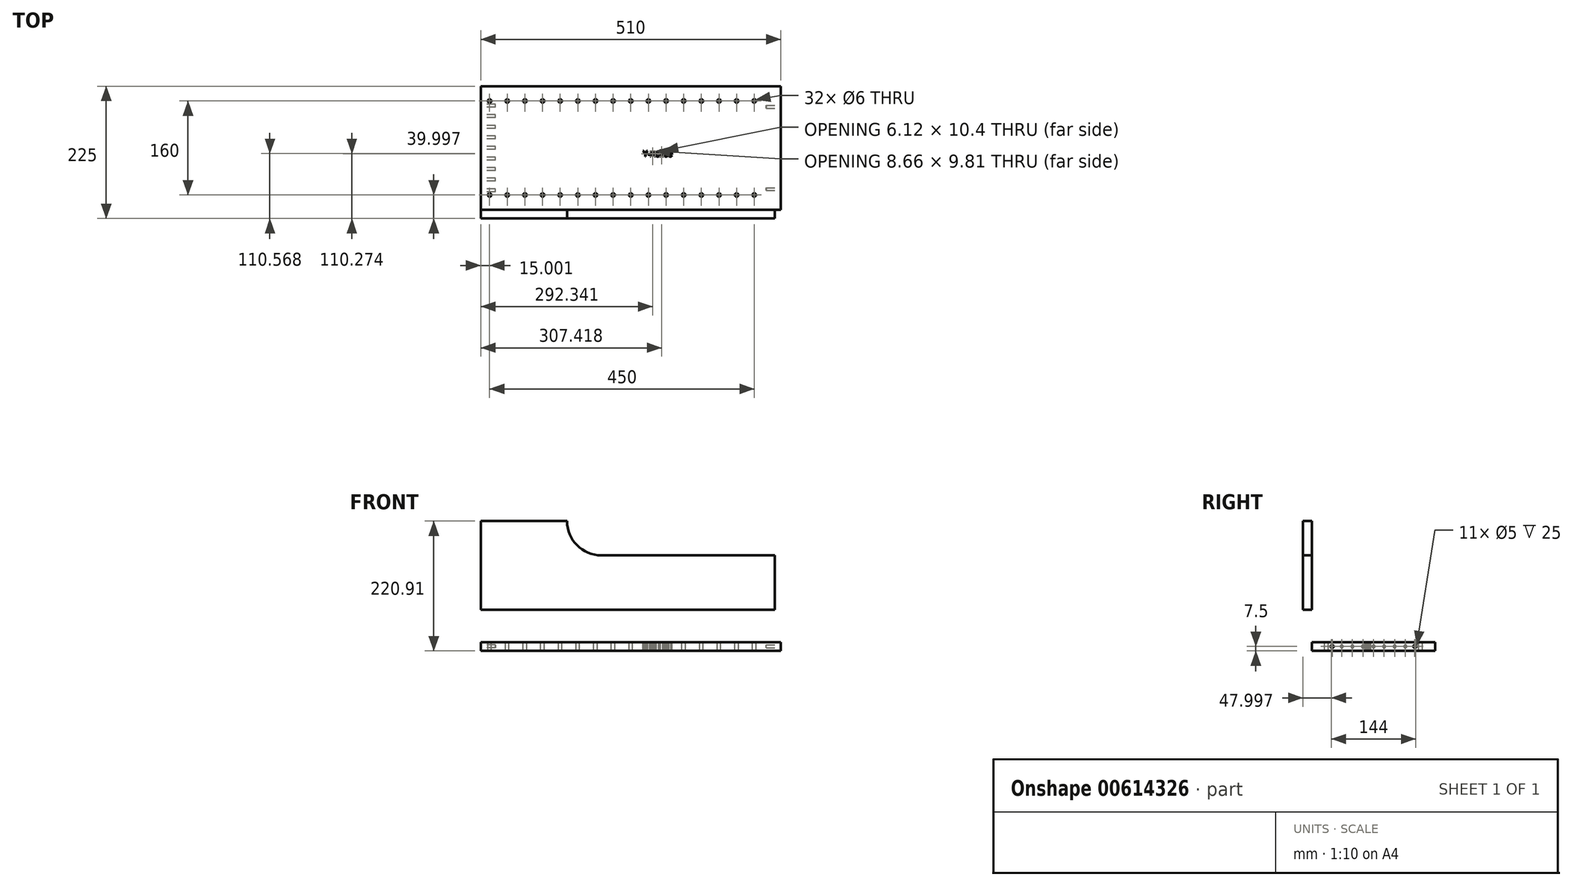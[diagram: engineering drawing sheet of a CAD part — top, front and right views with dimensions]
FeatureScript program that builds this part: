
annotation { "Feature Type Name" : "Feature", "Feature Type Description" : "" }
export const myFeature = defineFeature(function(context is Context, id is Id, definition is map)
    precondition{}
    {
        {
            var Q0;
            Q0=qCreatedBy(makeId("Top.planeOp"),FACE);
            var sketch = newSketch(context, id + "F0", { "sketchPlane" : qUnion([Q0])});
            skLineSegment(sketch, "E0.bottom", {"start": v(2.5, 35.14) * mm, "end": v(512.5, 35.14) * mm});
            skLineSegment(sketch, "E0.top", {"start": v(2.5, 245.14) * mm, "end": v(512.5, 245.14) * mm});
            skLineSegment(sketch, "E0.left", {"start": v(2.5, 35.14) * mm, "end": v(2.5, 245.14) * mm});
            skLineSegment(sketch, "E0.right", {"start": v(512.5, 35.14) * mm, "end": v(512.5, 245.14) * mm});
            skCircle(sketch, "E1", {"center": v(17.5, 60.14) * mm, "radius": 3 * mm});
            skCircle(sketch, "E2.0.1.1", {"center": v(17.5, 220.14) * mm, "radius": 3 * mm});
            skCircle(sketch, "E2.1.0.1", {"center": v(47.5, 60.14) * mm, "radius": 3 * mm});
            skCircle(sketch, "E2.1.1.1", {"center": v(47.5, 220.14) * mm, "radius": 3 * mm});
            skCircle(sketch, "E2.2.0.1", {"center": v(77.5, 60.14) * mm, "radius": 3 * mm});
            skCircle(sketch, "E2.2.1.1", {"center": v(77.5, 220.14) * mm, "radius": 3 * mm});
            skCircle(sketch, "E2.3.0.1", {"center": v(107.5, 60.14) * mm, "radius": 3 * mm});
            skCircle(sketch, "E2.3.1.1", {"center": v(107.5, 220.14) * mm, "radius": 3 * mm});
            skCircle(sketch, "E2.4.0.1", {"center": v(137.5, 60.14) * mm, "radius": 3 * mm});
            skCircle(sketch, "E2.4.1.1", {"center": v(137.5, 220.14) * mm, "radius": 3 * mm});
            skCircle(sketch, "E2.5.0.1", {"center": v(167.5, 60.14) * mm, "radius": 3 * mm});
            skCircle(sketch, "E2.5.1.1", {"center": v(167.5, 220.14) * mm, "radius": 3 * mm});
            skCircle(sketch, "E2.6.0.1", {"center": v(197.5, 60.14) * mm, "radius": 3 * mm});
            skCircle(sketch, "E2.6.1.1", {"center": v(197.5, 220.14) * mm, "radius": 3 * mm});
            skCircle(sketch, "E2.7.0.1", {"center": v(227.5, 60.14) * mm, "radius": 3 * mm});
            skCircle(sketch, "E2.7.1.1", {"center": v(227.5, 220.14) * mm, "radius": 3 * mm});
            skCircle(sketch, "E2.8.0.1", {"center": v(257.5, 60.14) * mm, "radius": 3 * mm});
            skCircle(sketch, "E2.8.1.1", {"center": v(257.5, 220.14) * mm, "radius": 3 * mm});
            skCircle(sketch, "E2.9.0.1", {"center": v(287.5, 60.14) * mm, "radius": 3 * mm});
            skCircle(sketch, "E2.9.1.1", {"center": v(287.5, 220.14) * mm, "radius": 3 * mm});
            skCircle(sketch, "E2.10.0.1", {"center": v(317.5, 60.14) * mm, "radius": 3 * mm});
            skCircle(sketch, "E2.10.1.1", {"center": v(317.5, 220.14) * mm, "radius": 3 * mm});
            skCircle(sketch, "E2.11.0.1", {"center": v(347.5, 60.14) * mm, "radius": 3 * mm});
            skCircle(sketch, "E2.11.1.1", {"center": v(347.5, 220.14) * mm, "radius": 3 * mm});
            skCircle(sketch, "E2.12.0.1", {"center": v(377.5, 60.14) * mm, "radius": 3 * mm});
            skCircle(sketch, "E2.12.1.1", {"center": v(377.5, 220.14) * mm, "radius": 3 * mm});
            skCircle(sketch, "E2.13.0.1", {"center": v(407.5, 60.14) * mm, "radius": 3 * mm});
            skCircle(sketch, "E2.13.1.1", {"center": v(407.5, 220.14) * mm, "radius": 3 * mm});
            skCircle(sketch, "E2.14.0.1", {"center": v(437.5, 60.14) * mm, "radius": 3 * mm});
            skCircle(sketch, "E2.14.1.1", {"center": v(437.5, 220.14) * mm, "radius": 3 * mm});
            skLineSegment(sketch, "E2.direction1", {"start": v(17.5, 60.14) * mm, "end": v(47.5, 60.14) * mm, "construction": true});
            skLineSegment(sketch, "E2.direction2", {"start": v(17.5, 60.14) * mm, "end": v(17.5, 220.14) * mm, "construction": true});
            skText(sketch, "E3", { "text": "Y-Achse", "fontName": "OpenSans-Regular.ttf"});
            skCircle(sketch, "E4.2.15.0", {"center": v(467.5, 60.14) * mm, "radius": 3 * mm});
            skCircle(sketch, "E4.2.15.1", {"center": v(467.5, 220.14) * mm, "radius": 3 * mm});
            skPoint(sketch, "E5", {"position": v(17.5, 140.14) * mm});
            skPoint(sketch, "E6", {"position": v(2.5, 140.14) * mm});
            const initialGuessF0  = {"E3": [0.27844, 0.12551, 1, 0, 0.00985]};
            skSetInitialGuess(sketch, initialGuessF0);
            skSolve(sketch);
        }
        {
            var Q0;
            Q0=makeQuery(id+"F0.imprint","IMPRINT",FACE,{"disambiguationData":[TD([[makeQuery(id+"F0.imprint","IMPRINT",EDGE,{"derivedFrom":sQuery(id+"F0.wireOp",EDGE,"E1")}),-1.0]])]});
            var Q1;
            Q1=makeQuery(id+"F0.imprint","IMPRINT",FACE,{"disambiguationData":[TD([[makeQuery(id+"F0.imprint","IMPRINT",EDGE,{"derivedFrom":sQuery(id+"F0.wireOp",EDGE,"E2.1.0.0")}),1.0]])]});
            var Q2;
            Q2=makeQuery(id+"F0.imprint","IMPRINT",FACE,{"disambiguationData":[TD([[makeQuery(id+"F0.imprint","IMPRINT",EDGE,{"derivedFrom":sQuery(id+"F0.wireOp",EDGE,"E2.2.0.0")}),1.0]])]});
            var Q3;
            Q3=makeQuery(id+"F0.imprint","IMPRINT",FACE,{"disambiguationData":[TD([[makeQuery(id+"F0.imprint","IMPRINT",EDGE,{"derivedFrom":sQuery(id+"F0.wireOp",EDGE,"E2.3.0.0")}),1.0]])]});
            var Q4;
            Q4=makeQuery(id+"F0.imprint","IMPRINT",FACE,{"disambiguationData":[TD([[makeQuery(id+"F0.imprint","IMPRINT",EDGE,{"derivedFrom":sQuery(id+"F0.wireOp",EDGE,"E2.0.1.0")}),1.0]])]});
            var Q5;
            Q5=makeQuery(id+"F0.imprint","IMPRINT",FACE,{"disambiguationData":[TD([[makeQuery(id+"F0.imprint","IMPRINT",EDGE,{"derivedFrom":sQuery(id+"F0.wireOp",EDGE,"E2.1.1.0")}),1.0]])]});
            var Q6;
            Q6=makeQuery(id+"F0.imprint","IMPRINT",FACE,{"disambiguationData":[TD([[makeQuery(id+"F0.imprint","IMPRINT",EDGE,{"derivedFrom":sQuery(id+"F0.wireOp",EDGE,"E2.2.1.0")}),1.0]])]});
            var Q7;
            Q7=makeQuery(id+"F0.imprint","IMPRINT",FACE,{"disambiguationData":[TD([[makeQuery(id+"F0.imprint","IMPRINT",EDGE,{"derivedFrom":sQuery(id+"F0.wireOp",EDGE,"E2.3.1.0")}),1.0]])]});
            var Q8;
            Q8=makeQuery(id+"F0.imprint","IMPRINT",FACE,{"disambiguationData":[TD([[makeQuery(id+"F0.imprint","IMPRINT",EDGE,{"derivedFrom":sQuery(id+"F0.wireOp",EDGE,"E2.4.1.0")}),1.0]])]});
            var Q9;
            Q9=makeQuery(id+"F0.imprint","IMPRINT",FACE,{"disambiguationData":[TD([[makeQuery(id+"F0.imprint","IMPRINT",EDGE,{"derivedFrom":sQuery(id+"F0.wireOp",EDGE,"E2.5.1.0")}),1.0]])]});
            var Q10;
            Q10=makeQuery(id+"F0.imprint","IMPRINT",FACE,{"disambiguationData":[TD([[makeQuery(id+"F0.imprint","IMPRINT",EDGE,{"derivedFrom":sQuery(id+"F0.wireOp",EDGE,"E2.6.1.0")}),1.0]])]});
            var Q11;
            Q11=makeQuery(id+"F0.imprint","IMPRINT",FACE,{"disambiguationData":[TD([[makeQuery(id+"F0.imprint","IMPRINT",EDGE,{"derivedFrom":sQuery(id+"F0.wireOp",EDGE,"E2.7.1.0")}),1.0]])]});
            var Q12;
            Q12=makeQuery(id+"F0.imprint","IMPRINT",FACE,{"disambiguationData":[TD([[makeQuery(id+"F0.imprint","IMPRINT",EDGE,{"derivedFrom":sQuery(id+"F0.wireOp",EDGE,"E2.8.1.0")}),1.0]])]});
            var Q13;
            Q13=makeQuery(id+"F0.imprint","IMPRINT",FACE,{"disambiguationData":[TD([[makeQuery(id+"F0.imprint","IMPRINT",EDGE,{"derivedFrom":sQuery(id+"F0.wireOp",EDGE,"E2.10.1.0")}),1.0]])]});
            var Q14;
            Q14=makeQuery(id+"F0.imprint","IMPRINT",FACE,{"disambiguationData":[TD([[makeQuery(id+"F0.imprint","IMPRINT",EDGE,{"derivedFrom":sQuery(id+"F0.wireOp",EDGE,"E2.9.1.0")}),1.0]])]});
            var Q15;
            Q15=makeQuery(id+"F0.imprint","IMPRINT",FACE,{"disambiguationData":[TD([[makeQuery(id+"F0.imprint","IMPRINT",EDGE,{"derivedFrom":sQuery(id+"F0.wireOp",EDGE,"E2.11.1.0")}),1.0]])]});
            var Q16;
            Q16=makeQuery(id+"F0.imprint","IMPRINT",FACE,{"disambiguationData":[TD([[makeQuery(id+"F0.imprint","IMPRINT",EDGE,{"derivedFrom":sQuery(id+"F0.wireOp",EDGE,"E2.12.1.0")}),1.0]])]});
            var Q17;
            Q17=makeQuery(id+"F0.imprint","IMPRINT",FACE,{"disambiguationData":[TD([[makeQuery(id+"F0.imprint","IMPRINT",EDGE,{"derivedFrom":sQuery(id+"F0.wireOp",EDGE,"E2.13.1.0")}),1.0]])]});
            var Q18;
            Q18=makeQuery(id+"F0.imprint","IMPRINT",FACE,{"disambiguationData":[TD([[makeQuery(id+"F0.imprint","IMPRINT",EDGE,{"derivedFrom":sQuery(id+"F0.wireOp",EDGE,"E2.14.1.0")}),1.0]])]});
            var Q19;
            Q19=makeQuery(id+"F0.imprint","IMPRINT",FACE,{"disambiguationData":[TD([[makeQuery(id+"F0.imprint","IMPRINT",EDGE,{"derivedFrom":sQuery(id+"F0.wireOp",EDGE,"E2.15.1.0")}),1.0]])]});
            var Q20;
            Q20=makeQuery(id+"F0.imprint","IMPRINT",FACE,{"disambiguationData":[TD([[makeQuery(id+"F0.imprint","IMPRINT",EDGE,{"derivedFrom":sQuery(id+"F0.wireOp",EDGE,"E2.16.1.0")}),1.0]])]});
            var Q21;
            Q21=makeQuery(id+"F0.imprint","IMPRINT",FACE,{"disambiguationData":[TD([[makeQuery(id+"F0.imprint","IMPRINT",EDGE,{"derivedFrom":sQuery(id+"F0.wireOp",EDGE,"E2.17.1.0")}),1.0]])]});
            var Q22;
            Q22=makeQuery(id+"F0.imprint","IMPRINT",FACE,{"disambiguationData":[TD([[makeQuery(id+"F0.imprint","IMPRINT",EDGE,{"derivedFrom":sQuery(id+"F0.wireOp",EDGE,"E2.18.1.0")}),1.0]])]});
            var Q23;
            Q23=makeQuery(id+"F0.imprint","IMPRINT",FACE,{"disambiguationData":[TD([[makeQuery(id+"F0.imprint","IMPRINT",EDGE,{"derivedFrom":sQuery(id+"F0.wireOp",EDGE,"E2.19.1.0")}),1.0]])]});
            var Q24;
            Q24=makeQuery(id+"F0.imprint","IMPRINT",FACE,{"disambiguationData":[TD([[makeQuery(id+"F0.imprint","IMPRINT",EDGE,{"derivedFrom":sQuery(id+"F0.wireOp",EDGE,"E2.19.0.0")}),1.0]])]});
            var Q25;
            Q25=makeQuery(id+"F0.imprint","IMPRINT",FACE,{"disambiguationData":[TD([[makeQuery(id+"F0.imprint","IMPRINT",EDGE,{"derivedFrom":sQuery(id+"F0.wireOp",EDGE,"E2.18.0.0")}),1.0]])]});
            var Q26;
            Q26=makeQuery(id+"F0.imprint","IMPRINT",FACE,{"disambiguationData":[TD([[makeQuery(id+"F0.imprint","IMPRINT",EDGE,{"derivedFrom":sQuery(id+"F0.wireOp",EDGE,"E2.17.0.0")}),1.0]])]});
            var Q27;
            Q27=makeQuery(id+"F0.imprint","IMPRINT",FACE,{"disambiguationData":[TD([[makeQuery(id+"F0.imprint","IMPRINT",EDGE,{"derivedFrom":sQuery(id+"F0.wireOp",EDGE,"E2.16.0.0")}),1.0]])]});
            var Q28;
            Q28=makeQuery(id+"F0.imprint","IMPRINT",FACE,{"disambiguationData":[TD([[makeQuery(id+"F0.imprint","IMPRINT",EDGE,{"derivedFrom":sQuery(id+"F0.wireOp",EDGE,"E2.15.0.0")}),1.0]])]});
            var Q29;
            Q29=makeQuery(id+"F0.imprint","IMPRINT",FACE,{"disambiguationData":[TD([[makeQuery(id+"F0.imprint","IMPRINT",EDGE,{"derivedFrom":sQuery(id+"F0.wireOp",EDGE,"E2.14.0.0")}),1.0]])]});
            var Q30;
            Q30=makeQuery(id+"F0.imprint","IMPRINT",FACE,{"disambiguationData":[TD([[makeQuery(id+"F0.imprint","IMPRINT",EDGE,{"derivedFrom":sQuery(id+"F0.wireOp",EDGE,"E2.13.0.0")}),1.0]])]});
            var Q31;
            Q31=makeQuery(id+"F0.imprint","IMPRINT",FACE,{"disambiguationData":[TD([[makeQuery(id+"F0.imprint","IMPRINT",EDGE,{"derivedFrom":sQuery(id+"F0.wireOp",EDGE,"E2.12.0.0")}),1.0]])]});
            var Q32;
            Q32=makeQuery(id+"F0.imprint","IMPRINT",FACE,{"disambiguationData":[TD([[makeQuery(id+"F0.imprint","IMPRINT",EDGE,{"derivedFrom":sQuery(id+"F0.wireOp",EDGE,"E2.11.0.0")}),1.0]])]});
            var Q33;
            Q33=makeQuery(id+"F0.imprint","IMPRINT",FACE,{"disambiguationData":[TD([[makeQuery(id+"F0.imprint","IMPRINT",EDGE,{"derivedFrom":sQuery(id+"F0.wireOp",EDGE,"E2.10.0.0")}),1.0]])]});
            var Q34;
            Q34=makeQuery(id+"F0.imprint","IMPRINT",FACE,{"disambiguationData":[TD([[makeQuery(id+"F0.imprint","IMPRINT",EDGE,{"derivedFrom":sQuery(id+"F0.wireOp",EDGE,"E2.9.0.0")}),1.0]])]});
            var Q35;
            Q35=makeQuery(id+"F0.imprint","IMPRINT",FACE,{"disambiguationData":[TD([[makeQuery(id+"F0.imprint","IMPRINT",EDGE,{"derivedFrom":sQuery(id+"F0.wireOp",EDGE,"E2.8.0.0")}),1.0]])]});
            var Q36;
            Q36=makeQuery(id+"F0.imprint","IMPRINT",FACE,{"disambiguationData":[TD([[makeQuery(id+"F0.imprint","IMPRINT",EDGE,{"derivedFrom":sQuery(id+"F0.wireOp",EDGE,"E2.7.0.0")}),1.0]])]});
            var Q37;
            Q37=makeQuery(id+"F0.imprint","IMPRINT",FACE,{"disambiguationData":[TD([[makeQuery(id+"F0.imprint","IMPRINT",EDGE,{"derivedFrom":sQuery(id+"F0.wireOp",EDGE,"E2.6.0.0")}),1.0]])]});
            var Q38;
            Q38=makeQuery(id+"F0.imprint","IMPRINT",FACE,{"disambiguationData":[TD([[makeQuery(id+"F0.imprint","IMPRINT",EDGE,{"derivedFrom":sQuery(id+"F0.wireOp",EDGE,"E2.5.0.0")}),1.0]])]});
            var Q39;
            Q39=makeQuery(id+"F0.imprint","IMPRINT",FACE,{"disambiguationData":[TD([[makeQuery(id+"F0.imprint","IMPRINT",EDGE,{"derivedFrom":sQuery(id+"F0.wireOp",EDGE,"E2.4.0.0")}),1.0]])]});
            var Q40;
            Q40=makeQuery(id+"F0.imprint","IMPRINT",FACE,{"disambiguationData":[TD([[makeQuery(id+"F0.imprint","IMPRINT",EDGE,{"derivedFrom":sQuery(id+"F0.wireOp",EDGE,"E0.bottom")}),1.0]])]});
            extrude(context, id + "F1", {"entities" : qUnion([Q0, Q1, Q2, Q3, Q4, Q5, Q6, Q7, Q8, Q9, Q10, Q11, Q12, Q13, Q14, Q15, Q16, Q17, Q18, Q19, Q20, Q21, Q22, Q23, Q24, Q25, Q26, Q27, Q28, Q29, Q30, Q31, Q32, Q33, Q34, Q35, Q36, Q37, Q38, Q39, Q40]), "oppositeDirection" : true, "depth" : 15 * mm, "offsetDistance" : 25 * mm});
        }
        {
            var Q0;
            Q0=makeQuery(id+"F1.opExtrude","SWEPT_FACE",FACE,{"disambiguationData":[OSD([sQuery(id+"F0.wireOp",EDGE,"E0.right")])]});
            var sketch = newSketch(context, id + "F2", { "sketchPlane" : qUnion([Q0])});
            skCircle(sketch, "E7", {"center": v(70.14, -7.5) * mm, "radius": 2.5 * mm});
            skCircle(sketch, "E8", {"center": v(210.14, -7.5) * mm, "radius": 2.5 * mm});
            skSolve(sketch);
        }
        {
            var Q0;
            Q0=makeQuery(id+"F2.imprint","IMPRINT",FACE,{"disambiguationData":[TD([[makeQuery(id+"F2.imprint","IMPRINT",EDGE,{"derivedFrom":sQuery(id+"F2.wireOp",EDGE,"E7")}),1.0]])]});
            var Q1;
            Q1=makeQuery(id+"F2.imprint","IMPRINT",FACE,{"disambiguationData":[TD([[makeQuery(id+"F2.imprint","IMPRINT",EDGE,{"derivedFrom":sQuery(id+"F2.wireOp",EDGE,"E8")}),1.0]])]});
            extrude(context, id + "F3", {"entities" : qUnion([Q0, Q1]), "operationType" : NewBodyOperationType.REMOVE, "oppositeDirection" : true, "depth" : 25 * mm, "offsetDistance" : 25 * mm});
        }
        {
            var Q0;
            Q0=makeQuery(id+"F1.opExtrude","SWEPT_FACE",FACE,{"disambiguationData":[OSD([sQuery(id+"F0.wireOp",EDGE,"E0.left")])]});
            var sketch = newSketch(context, id + "F4", { "sketchPlane" : qUnion([Q0])});
            skCircle(sketch, "E9", {"center": v(-212.14, -7.5) * mm, "radius": 2.5 * mm});
            skPoint(sketch, "E10", {"position": v(-35.14, -7.5) * mm});
            skPoint(sketch, "E11", {"position": v(-140.14, -15) * mm});
            skCircle(sketch, "E12.1.0.0", {"center": v(-194.14, -7.5) * mm, "radius": 2.5 * mm});
            skCircle(sketch, "E12.2.0.0", {"center": v(-176.14, -7.5) * mm, "radius": 2.5 * mm});
            skCircle(sketch, "E12.3.0.0", {"center": v(-158.14, -7.5) * mm, "radius": 2.5 * mm});
            skCircle(sketch, "E12.4.0.0", {"center": v(-140.14, -7.5) * mm, "radius": 2.5 * mm});
            skCircle(sketch, "E12.5.0.0", {"center": v(-122.14, -7.5) * mm, "radius": 2.5 * mm});
            skLineSegment(sketch, "E12.direction1", {"start": v(-212.14, -7.5) * mm, "end": v(-194.14, -7.5) * mm, "construction": true});
            skLineSegment(sketch, "E13", {"start": v(-140.14, -15) * mm, "end": v(-140.14, 0) * mm, "construction": true});
            skCircle(sketch, "E14.0.6.0", {"center": v(-104.14, -7.5) * mm, "radius": 2.5 * mm});
            skCircle(sketch, "E15.0.7.0", {"center": v(-86.14, -7.5) * mm, "radius": 2.5 * mm});
            skCircle(sketch, "E16.0.8.0", {"center": v(-68.14, -7.5) * mm, "radius": 2.5 * mm});
            skSolve(sketch);
        }
        {
            var Q0;
            Q0=makeQuery(id+"F4.imprint","IMPRINT",FACE,{"disambiguationData":[TD([[makeQuery(id+"F4.imprint","IMPRINT",EDGE,{"derivedFrom":sQuery(id+"F4.wireOp",EDGE,"E9")}),1.0]])]});
            var Q1;
            Q1=makeQuery(id+"F4.imprint","IMPRINT",FACE,{"disambiguationData":[TD([[makeQuery(id+"F4.imprint","IMPRINT",EDGE,{"derivedFrom":sQuery(id+"F4.wireOp",EDGE,"E12.1.0.0")}),1.0]])]});
            var Q2;
            Q2=makeQuery(id+"F4.imprint","IMPRINT",FACE,{"disambiguationData":[TD([[makeQuery(id+"F4.imprint","IMPRINT",EDGE,{"derivedFrom":sQuery(id+"F4.wireOp",EDGE,"E12.2.0.0")}),1.0]])]});
            var Q3;
            Q3=makeQuery(id+"F4.imprint","IMPRINT",FACE,{"disambiguationData":[TD([[makeQuery(id+"F4.imprint","IMPRINT",EDGE,{"derivedFrom":sQuery(id+"F4.wireOp",EDGE,"E12.3.0.0")}),1.0]])]});
            var Q4;
            Q4=makeQuery(id+"F4.imprint","IMPRINT",FACE,{"disambiguationData":[TD([[makeQuery(id+"F4.imprint","IMPRINT",EDGE,{"derivedFrom":sQuery(id+"F4.wireOp",EDGE,"E12.4.0.0")}),1.0]])]});
            var Q5;
            Q5=makeQuery(id+"F4.imprint","IMPRINT",FACE,{"disambiguationData":[TD([[makeQuery(id+"F4.imprint","IMPRINT",EDGE,{"derivedFrom":sQuery(id+"F4.wireOp",EDGE,"E12.5.0.0")}),1.0]])]});
            var Q6;
            Q6=makeQuery(id+"F4.imprint","IMPRINT",FACE,{"disambiguationData":[TD([[makeQuery(id+"F4.imprint","IMPRINT",EDGE,{"derivedFrom":sQuery(id+"F4.wireOp",EDGE,"E14.0.6.0")}),1.0]])]});
            var Q7;
            Q7=makeQuery(id+"F4.imprint","IMPRINT",FACE,{"disambiguationData":[TD([[makeQuery(id+"F4.imprint","IMPRINT",EDGE,{"derivedFrom":sQuery(id+"F4.wireOp",EDGE,"E15.0.7.0")}),1.0]])]});
            var Q8;
            Q8=makeQuery(id+"F4.imprint","IMPRINT",FACE,{"disambiguationData":[TD([[makeQuery(id+"F4.imprint","IMPRINT",EDGE,{"derivedFrom":sQuery(id+"F4.wireOp",EDGE,"E16.0.8.0")}),1.0]])]});
            extrude(context, id + "F5", {"entities" : qUnion([Q0, Q1, Q2, Q3, Q4, Q5, Q6, Q7, Q8]), "operationType" : NewBodyOperationType.REMOVE, "oppositeDirection" : true, "depth" : 25 * mm, "offsetDistance" : 25 * mm});
        }
        {
            var Q0;
            Q0=makeQuery(id+"F1.opExtrude","SWEPT_FACE",FACE,{"disambiguationData":[OSD([sQuery(id+"F0.wireOp",EDGE,"E0.bottom")])]});
            var sketch = newSketch(context, id + "F6", { "sketchPlane" : qUnion([Q0])});
            skPoint(sketch, "E17.centerSnap0", {"position": v(2.5, -7.5) * mm});
            skLineSegment(sketch, "E18.bottom", {"start": v(2.5, 205.9) * mm, "end": v(149.14, 205.9) * mm});
            skLineSegment(sketch, "E18.top", {"start": v(2.5, 55.12) * mm, "end": v(502.5, 55.12) * mm});
            skLineSegment(sketch, "E18.left", {"start": v(2.5, 55.12) * mm, "end": v(2.5, 205.9) * mm});
            skLineSegment(sketch, "E18.right", {"start": v(502.5, 55.12) * mm, "end": v(502.5, 147.52) * mm});
            skLineSegment(sketch, "E19", {"start": v(502.5, 147.52) * mm, "end": v(207.53, 147.52) * mm});
            skArc(sketch, "E20", {"start": v(207.53, 147.52) * mm, "mid": v(166.24, 164.62) * mm, "end": v(149.14, 205.9) * mm});
            skSolve(sketch);
        }
        {
            var Q0;
            {var subQ3=sQuery(id+"F6.wireOp",EDGE,"E18.top");Q0=makeQuery(id+"F6.imprint","IMPRINT",FACE,{"disambiguationData":[TD([[makeQuery(id+"F6.imprint","IMPRINT",EDGE,{"derivedFrom":subQ3}),1.0]])]});}
            var Q1;
            Q1=makeQuery(id+"F6.imprint","IMPRINT",FACE,{"disambiguationData":[TD([[makeQuery(id+"F6.imprint","IMPRINT",EDGE,{"derivedFrom":sQuery(id+"F6.wireOp",EDGE,"BvxUVQRd-sD9S-NBgv-cZaA-1zXd1SBs2lkj")}),-1.0]])]});
            var Q2;
            Q2=makeQuery(id+"F6.imprint","IMPRINT",FACE,{"disambiguationData":[TD([[makeQuery(id+"F6.imprint","IMPRINT",EDGE,{"derivedFrom":sQuery(id+"F6.wireOp",EDGE,"b7ef3dc0-e442-43f9-b0e9-1a77a081d4e1.1.0.0")}),1.0]])]});
            var Q3;
            Q3=makeQuery(id+"F6.imprint","IMPRINT",FACE,{"disambiguationData":[TD([[makeQuery(id+"F6.imprint","IMPRINT",EDGE,{"derivedFrom":sQuery(id+"F6.wireOp",EDGE,"b7ef3dc0-e442-43f9-b0e9-1a77a081d4e1.2.0.0")}),1.0]])]});
            var Q4;
            Q4=makeQuery(id+"F6.imprint","IMPRINT",FACE,{"disambiguationData":[TD([[makeQuery(id+"F6.imprint","IMPRINT",EDGE,{"derivedFrom":sQuery(id+"F6.wireOp",EDGE,"b7ef3dc0-e442-43f9-b0e9-1a77a081d4e1.3.0.0")}),1.0]])]});
            var Q5;
            Q5=makeQuery(id+"F6.imprint","IMPRINT",FACE,{"disambiguationData":[TD([[makeQuery(id+"F6.imprint","IMPRINT",EDGE,{"derivedFrom":sQuery(id+"F6.wireOp",EDGE,"b7ef3dc0-e442-43f9-b0e9-1a77a081d4e1.4.0.0")}),1.0]])]});
            var Q6;
            Q6=makeQuery(id+"F6.imprint","IMPRINT",FACE,{"disambiguationData":[TD([[makeQuery(id+"F6.imprint","IMPRINT",EDGE,{"derivedFrom":sQuery(id+"F6.wireOp",EDGE,"b7ef3dc0-e442-43f9-b0e9-1a77a081d4e1.6.0.0")}),1.0]])]});
            var Q7;
            Q7=makeQuery(id+"F6.imprint","IMPRINT",FACE,{"disambiguationData":[TD([[makeQuery(id+"F6.imprint","IMPRINT",EDGE,{"derivedFrom":sQuery(id+"F6.wireOp",EDGE,"b7ef3dc0-e442-43f9-b0e9-1a77a081d4e1.5.0.0")}),1.0]])]});
            var Q8;
            Q8=makeQuery(id+"F6.imprint","IMPRINT",FACE,{"disambiguationData":[TD([[makeQuery(id+"F6.imprint","IMPRINT",EDGE,{"derivedFrom":sQuery(id+"F6.wireOp",EDGE,"b7ef3dc0-e442-43f9-b0e9-1a77a081d4e1.8.0.0")}),1.0]])]});
            var Q9;
            Q9=makeQuery(id+"F6.imprint","IMPRINT",FACE,{"disambiguationData":[TD([[makeQuery(id+"F6.imprint","IMPRINT",EDGE,{"derivedFrom":sQuery(id+"F6.wireOp",EDGE,"b7ef3dc0-e442-43f9-b0e9-1a77a081d4e1.7.0.0")}),1.0]])]});
            extrude(context, id + "F7", {"entities" : qUnion([Q0, Q1, Q2, Q3, Q4, Q5, Q6, Q7, Q8, Q9]), "depth" : 15 * mm, "offsetDistance" : 25 * mm});
        }
    });
